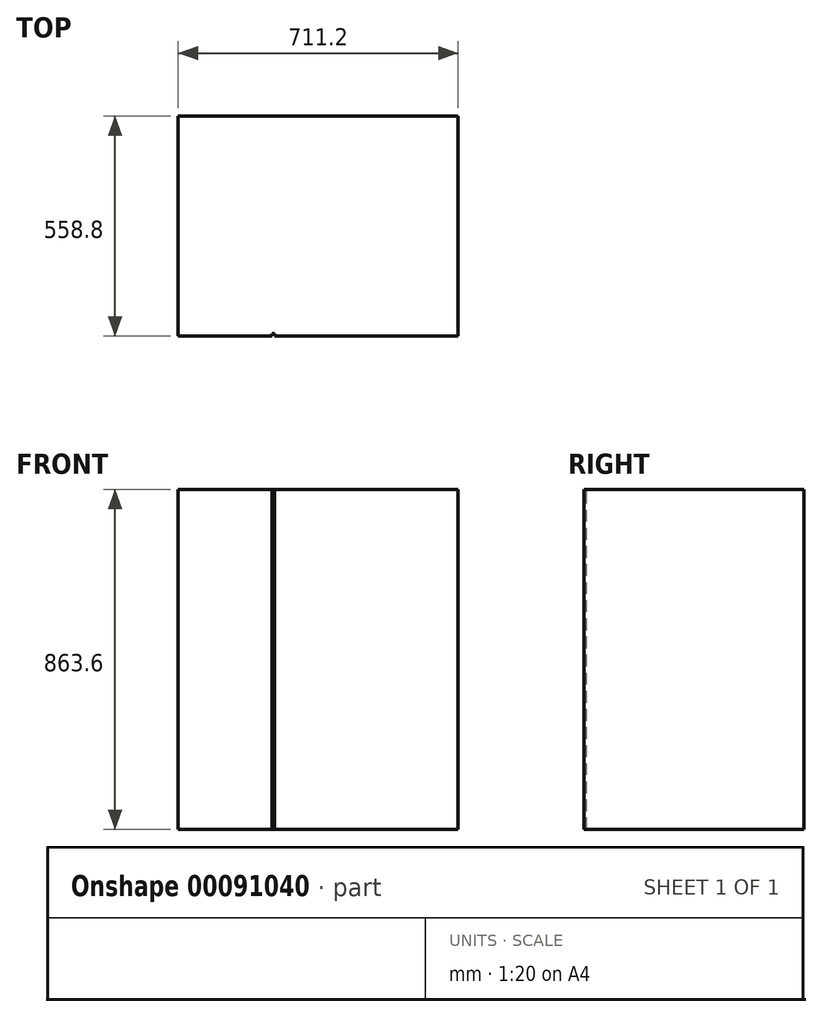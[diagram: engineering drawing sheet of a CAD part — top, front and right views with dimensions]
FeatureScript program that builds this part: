
annotation { "Feature Type Name" : "Feature", "Feature Type Description" : "" }
export const myFeature = defineFeature(function(context is Context, id is Id, definition is map)
    precondition{}
    {
        {
            var Q0;
            Q0=qCreatedBy(makeId("Front.planeOp"),FACE);
            var sketch = newSketch(context, id + "F0", { "sketchPlane" : qUnion([Q0])});
            skLineSegment(sketch, "E0.bottom", {"start": v(-360.4, 441.24) * mm, "end": v(350.8, 441.24) * mm});
            skLineSegment(sketch, "E0.top", {"start": v(-360.4, -422.36) * mm, "end": v(350.8, -422.36) * mm});
            skLineSegment(sketch, "E0.left", {"start": v(-360.4, 441.24) * mm, "end": v(-360.4, -422.36) * mm});
            skLineSegment(sketch, "E0.right", {"start": v(350.8, 441.24) * mm, "end": v(350.8, -422.36) * mm});
            skLineSegment(sketch, "E1", {"start": v(-119.1, 441.24) * mm, "end": v(-119.1, -422.36) * mm, "construction": true});
            skSolve(sketch);
        }
        {
            var Q0;
            Q0 = qSketchRegion(id + "F0", true);
            extrude(context, id + "F1", {"entities" : qUnion([Q0]), "depth" : 558.8 * mm});
        }
        {
            var Q0;
            Q0=makeQuery(id+"F1.opExtrude","SWEPT_FACE",FACE,{"disambiguationData":[OSD([sQuery(id+"F0.wireOp",EDGE,"E0.bottom")])]});
            var sketch = newSketch(context, id + "F2", { "sketchPlane" : qUnion([Q0])});
            skLineSegment(sketch, "E2.bottom", {"start": v(-115.93, -558.8) * mm, "end": v(-122.28, -558.8) * mm});
            skLineSegment(sketch, "E2.top", {"start": v(-115.93, -552.45) * mm, "end": v(-122.28, -552.45) * mm});
            skLineSegment(sketch, "E2.left", {"start": v(-115.93, -558.8) * mm, "end": v(-115.93, -552.45) * mm});
            skLineSegment(sketch, "E2.right", {"start": v(-122.28, -558.8) * mm, "end": v(-122.28, -552.45) * mm});
            skPoint(sketch, "E3", {"position": v(-119.1, -558.8) * mm});
            skSolve(sketch);
        }
        {
            var Q0;
            Q0 = qSketchRegion(id + "F2", true);
            extrude(context, id + "F3", {"entities" : qUnion([Q0]), "operationType" : NewBodyOperationType.REMOVE, "endBound" : BoundingType.THROUGH_ALL, "oppositeDirection" : true, "depth" : 25.4 * mm});
        }
    });
